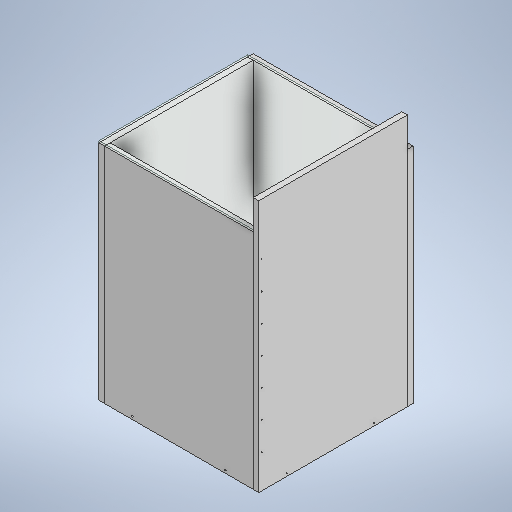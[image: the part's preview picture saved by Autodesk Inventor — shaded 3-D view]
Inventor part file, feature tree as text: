
AUTODESK INVENTOR PART (.ipt)
format: ipt  version: 2025.1 (Build 291241000, 241)  size: 386,048 bytes
history: native  units: mm
features: other x24, extrude x13, sketch x13, imported_body x1
ambient origin geometry x8: Origin, YZ Plane, XZ Plane, XY Plane, X Axis, Y Axis, Z Axis, Center Point
bodies: Body1 (feature_tree), Body2 (feature_tree), Body3 (feature_tree), Body4 (feature_tree), Body5 (feature_tree), Body6 (feature_tree), Body7 (feature_tree)
feature tree (51):
  other  "parede 1"
  extrude  "Extrusão1"  Depth=600.0mm
  extrude  "Extrusão2"  Depth=300.0mm
  extrude  "Extrusão4"  Depth=400.0mm
  extrude  "Extrusão9"  Depth=15.0mm TaperAngle=0.0deg
  extrude  "Extrusão10"  Depth=400.0mm
  extrude  "Extrusão11"  Depth=15.0mm TaperAngle=0.0deg
  other  "Plano de trabalho1"
  extrude  "Extrusão12"  Depth=5.0mm
  extrude  "Extrusão13"  Depth=75.0mm TaperAngle=0.0deg
  extrude  "Extrusão14"  Depth=15.0mm TaperAngle=0.0deg
  extrude  "Extrusão15"  Depth=15.0mm TaperAngle=0.0deg
  extrude  "Extrusão16"  Depth=75.0mm
  extrude  "Extrusão17"  Depth=4.0mm
  extrude  "Extrusão18"  Depth=75.0mm TaperAngle=0.0deg
  sketch  "Esboço1"  dims[d0=400.0mm d1=600.0mm]
  sketch  "Esboço2"  dims[d2=200.0mm d3=300.0mm]
  other  "Contorno projetado1"
  other  "parede maior"
  sketch  "Esboço4"  dims[d4=15.0mm d5=0.0mm d7=400.0mm]
  other  "Contorno projetado5"
  other  "Contorno projetado6"
  other  "porta"
  sketch  "Esboço10"  dims[d8=15.0mm d9=0.0mm d12=15.0mm d13=0.0mm]
  other  "Contorno projetado17"
  other  "Contorno projetado18"
  other  "parede 2"
  sketch  "Esboço11"  dims[d29=15.0mm d30=0.0mm d31=400.0mm]
  sketch  "Esboço12"  dims[d32=80.0mm d33=15.0mm d34=0.0mm]
  other  "Contorno projetado19"
  other  "vidro"
  sketch  "Esboço15"  dims[d35=5.0mm d36=0.0mm d37=3.0mm]
  sketch  "Esboço16"  dims[d38=75.0mm d42=50000.0mm d43=0.0mm]
  other  "Contorno projetado23"
  other  "Contorno projetado24"
  other  "Contorno projetado25"
  other  "suporte vidro"
  sketch  "Esboço17"  dims[d44=40.0mm d45=15.0mm d46=0.0mm]
  other  "Contorno projetado26"
  other  "Contorno projetado27"
  other  "Contorno projetado28"
  other  "Contorno projetado29"
  sketch  "Esboço18"  dims[d47=15.0mm d48=0.0mm d49=15.0mm d50=0.0mm]
  other  "Contorno projetado30"
  other  "Contorno projetado31"
  other  "Contorno projetado32"
  imported_body  "base"
  other  "Contorno projetado33"
  sketch  "Esboço19"  dims[d51=4.0mm d52=75.0mm]
  sketch  "Esboço20"  dims[d53=7.5mm d54=4.0mm]
  sketch  "Esboço22"  dims[d55=75.0mm d56=5000.0mm d57=0.0mm d58=4.0mm d59=75.0mm d60=20.0mm d61=4.0mm d62=75.0mm d63=20.0mm d64=5000.0mm d65=0.0mm d66=7.5mm d67=7.5mm d70=3.0mm d71=7.5mm d72=75.0mm d82=3.0mm d83=75.0mm d84=7.5mm d85=3.0mm d86=75.0mm d87=3.0mm d88=75.0mm d89=3.0mm d90=75.0mm d91=3.0mm d92=75.0mm d93=3.0mm d94=75.0mm d95=3.0mm d96=75.0mm d97=50000.0mm d98=0.0mm d18=0.5mm d19=0.872665mm d20=0.5mm d21=0.872665mm d39=1.0mm d40=0.15mm d41=0.25mm]
